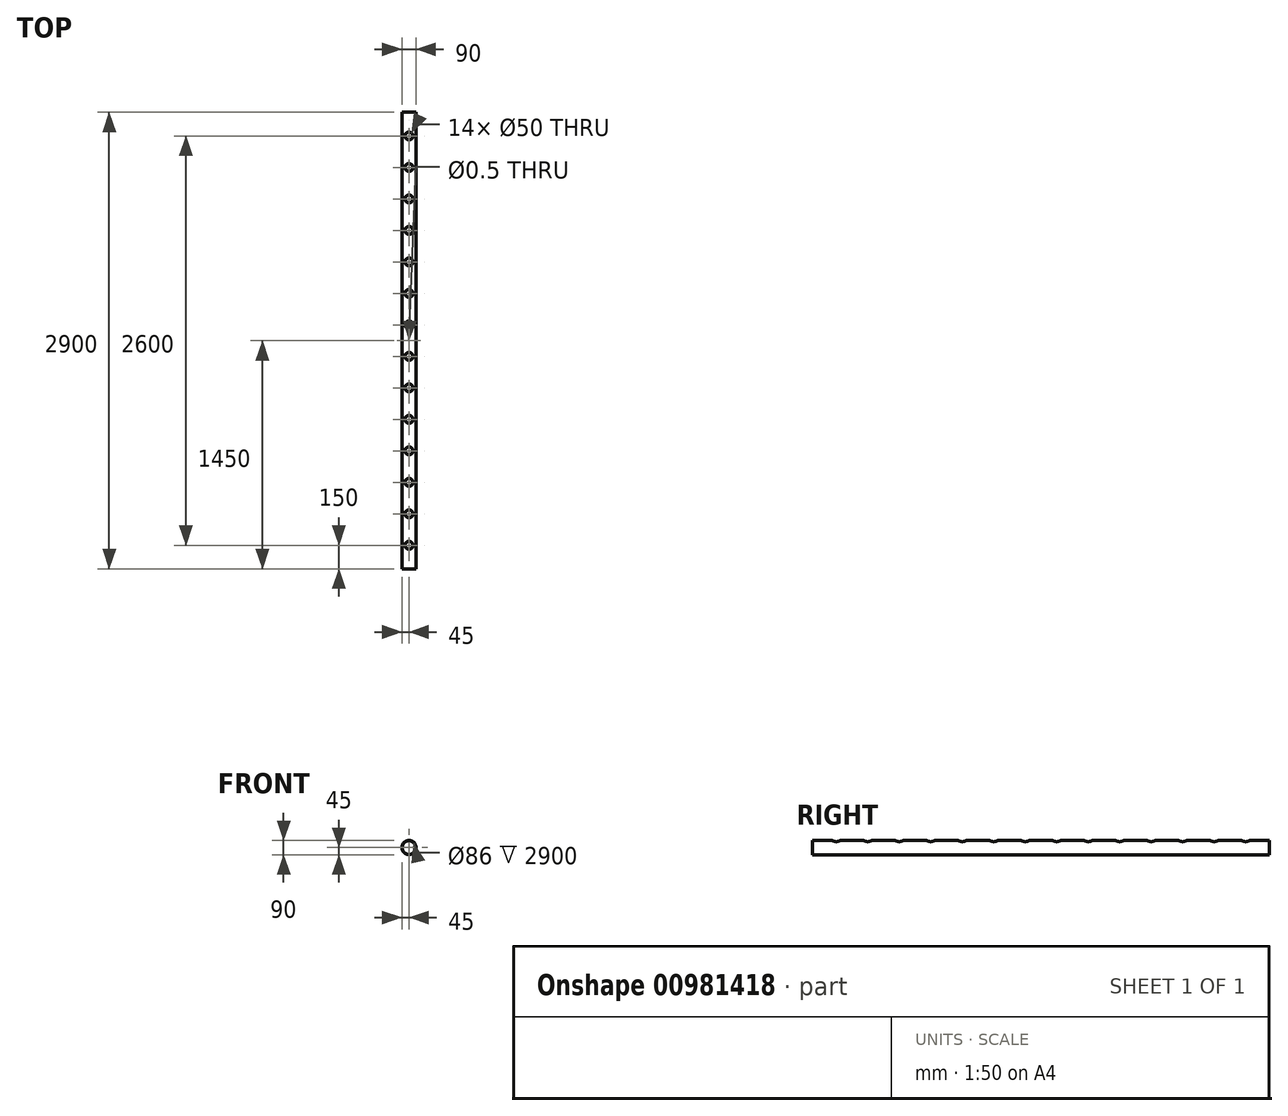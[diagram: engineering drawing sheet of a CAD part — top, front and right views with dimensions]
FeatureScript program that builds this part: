
annotation { "Feature Type Name" : "Feature", "Feature Type Description" : "" }
export const myFeature = defineFeature(function(context is Context, id is Id, definition is map)
    precondition{}
    {
        {
            var Q0;
            Q0=qCreatedBy(makeId("Front.planeOp"),FACE);
            var sketch = newSketch(context, id + "F0", { "sketchPlane" : qUnion([Q0])});
            skCircle(sketch, "E0", {"center": v(0, 0) * mm, "radius": 45 * mm});
            skCircle(sketch, "E1.0", {"center": v(0, 0) * mm, "radius": 43 * mm});
            skSolve(sketch);
        }
        {
            var Q0;
            Q0=qSketchRegion(id+"F0",true);
            extrude(context, id + "F1", {"entities" : qUnion([Q0]), "endBound" : BoundingType.SYMMETRIC, "depth" : 2900 * mm, "offsetDistance" : 25 * mm});
        }
        {
            var Q0;
            Q0=qCreatedBy(makeId("Top.planeOp"),FACE);
            cPlane(context, id + "F2", {"entities" : qUnion([Q0]), "cplaneType" : CPlaneType.OFFSET, "offset" : 45 * mm, "width" : 150 * mm, "height" : 150 * mm});
        }
        {
            var Q0;
            Q0=qCreatedBy(id+"F2.planeOp",FACE);
            var sketch = newSketch(context, id + "F3", { "sketchPlane" : qUnion([Q0])});
            skPoint(sketch, "E2", {"position": v(0, -1300) * mm});
            skPoint(sketch, "E3", {"position": v(0, -1100) * mm});
            skPoint(sketch, "E4", {"position": v(0, -900) * mm});
            skPoint(sketch, "E5", {"position": v(0, -700) * mm});
            skPoint(sketch, "E6", {"position": v(0, -500) * mm});
            skPoint(sketch, "E7", {"position": v(0, -300) * mm});
            skPoint(sketch, "E8", {"position": v(0, -100) * mm});
            skPoint(sketch, "E9", {"position": v(0, 100) * mm});
            skPoint(sketch, "E10", {"position": v(0, 300) * mm});
            skPoint(sketch, "E11", {"position": v(0, 500) * mm});
            skPoint(sketch, "E12", {"position": v(0, 700) * mm});
            skPoint(sketch, "E13", {"position": v(0, 900) * mm});
            skPoint(sketch, "E14", {"position": v(0, 1100) * mm});
            skPoint(sketch, "E15", {"position": v(0, 1300) * mm});
            skSolve(sketch);
        }
        {
            var Q0;
            Q0=sQuery(id+"F3.wireOp",VERTEX,"E2");
            var Q1;
            Q1=sQuery(id+"F3.wireOp",VERTEX,"E3");
            var Q2;
            Q2=sQuery(id+"F3.wireOp",VERTEX,"E4");
            var Q3;
            Q3=sQuery(id+"F3.wireOp",VERTEX,"E5");
            var Q4;
            Q4=sQuery(id+"F3.wireOp",VERTEX,"E6");
            var Q5;
            Q5=sQuery(id+"F3.wireOp",VERTEX,"E7");
            var Q6;
            Q6=sQuery(id+"F3.wireOp",VERTEX,"E8");
            var Q7;
            Q7=sQuery(id+"F3.wireOp",VERTEX,"E9");
            var Q8;
            Q8=sQuery(id+"F3.wireOp",VERTEX,"E10");
            var Q9;
            Q9=sQuery(id+"F3.wireOp",VERTEX,"E11");
            var Q10;
            Q10=sQuery(id+"F3.wireOp",VERTEX,"E12");
            var Q11;
            Q11=sQuery(id+"F3.wireOp",VERTEX,"E13");
            var Q12;
            Q12=sQuery(id+"F3.wireOp",VERTEX,"E14");
            var Q13;
            Q13=sQuery(id+"F3.wireOp",VERTEX,"E15");
            var Q14;
            Q14=sQuery(id+"F3.wireOp",VERTEX,"46e0f81d-7a3e-4eb5-89d9-9d338da62cf5");
            var Q15;
            Q15=sQuery(id+"F3.wireOp",VERTEX,"f4cd902c-7ee6-44a1-aa6d-15636b985a91");
            var Q16;
            Q16=sQuery(id+"F3.wireOp",VERTEX,"a0becd45-3f8c-473a-b9c5-eca89ffffb86");
            var Q17;
            Q17=sQuery(id+"F3.wireOp",VERTEX,"449d03d7-6090-459a-adaf-9611daa20e82");
            var Q18;
            Q18=sQuery(id+"F3.wireOp",VERTEX,"1d2369e2-f7b6-45cb-9ac7-ef4d2139859a");
            var Q19;
            Q19=sQuery(id+"F3.wireOp",VERTEX,"4217ffee-23aa-4e57-b56b-1031955cdd20");
            var Q20;
            Q20=sQuery(id+"F3.wireOp",VERTEX,"f9e667d2-43f0-46cb-85dd-7700daad2ab1");
            var Q21;
            Q21=sQuery(id+"F3.wireOp",VERTEX,"a141cc4f-d6fa-4136-a428-d91cc8b08e23");
            var Q22;
            Q22=sQuery(id+"F3.wireOp",VERTEX,"6950c5e6-caf7-4953-8c5b-56709a9cffe9");
            var Q23;
            Q23=sQuery(id+"F3.wireOp",VERTEX,"1581daf2-9304-4365-a3cc-e960652a3bf4");
            var Q24;
            Q24=sQuery(id+"F3.wireOp",VERTEX,"25a0b738-50ad-46bb-ba52-db4eb22869ea");
            var Q25;
            Q25=sQuery(id+"F3.wireOp",VERTEX,"23c6b068-1da5-4682-a93c-07f6e733a235");
            var Q26;
            Q26=sQuery(id+"F3.wireOp",VERTEX,"77491461-51bd-4097-a69a-b50156a0fef7");
            var Q27;
            Q27=sQuery(id+"F3.wireOp",VERTEX,"89e2eaf9-af87-4198-a739-5b01357332c3");
            var Q28;
            Q28=sQuery(id+"F3.wireOp",VERTEX,"a31ac070-19d1-4092-b391-6f630edb761b");
            var Q29;
            Q29=makeQuery(id+"F1.opExtrude","SWEPT_BODY",BODY,{"disambiguationData":[OSD([sQuery(id+"F0.wireOp",EDGE,"E0"),sQuery(id+"F0.wireOp",EDGE,"E1.0")])]});
            hole(context, id + "F4", {"style" : HoleStyle.SIMPLE, "endStyle" : HoleEndStyle.BLIND, "holeDiameter" : 50 * mm, "majorDiameter" : 5 * mm, "holeDepth" : 50 * mm, "isTappedThrough" : true, "tappedDepth" : 12 * mm, "tapClearance" : 3, "startFromSketch" : true, "locations" : qUnion([Q0, Q1, Q2, Q3, Q4, Q5, Q6, Q7, Q8, Q9, Q10, Q11, Q12, Q13, Q14, Q15, Q16, Q17, Q18, Q19, Q20, Q21, Q22, Q23, Q24, Q25, Q26, Q27, Q28]), "scope" : qUnion([Q29])});
        }
        {
            var Q0;
            Q0=qCreatedBy(makeId("Top.planeOp"),FACE);
            var sketch = newSketch(context, id + "F5", { "sketchPlane" : qUnion([Q0])});
            skPoint(sketch, "E16", {"position": v(0, 0) * mm});
            skSolve(sketch);
        }
        {
            var Q0;
            Q0=sQuery(id+"F5.wireOp",VERTEX,"E16");
            var Q1;
            Q1=makeQuery(id+"F1.opExtrude","SWEPT_BODY",BODY,{"disambiguationData":[OSD([sQuery(id+"F0.wireOp",EDGE,"E0"),sQuery(id+"F0.wireOp",EDGE,"E1.0")])]});
            hole(context, id + "F6", {"style" : HoleStyle.SIMPLE, "endStyle" : HoleEndStyle.BLIND, "holeDiameter" : 0.5 * mm, "majorDiameter" : 5 * mm, "holeDepth" : 50 * mm, "isTappedThrough" : true, "tappedDepth" : 12 * mm, "tapClearance" : 3, "startFromSketch" : true, "locations" : qUnion([Q0]), "scope" : qUnion([Q1])});
        }
    });
